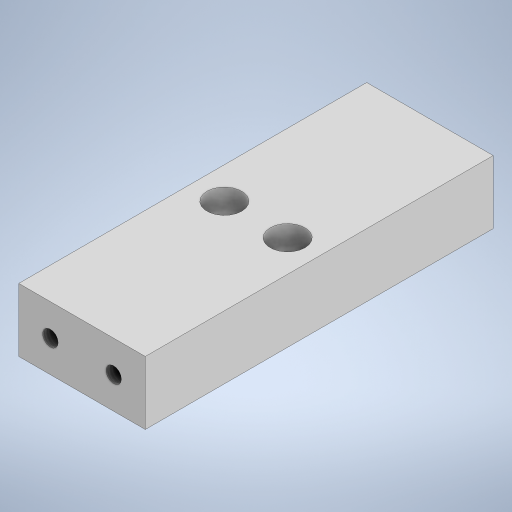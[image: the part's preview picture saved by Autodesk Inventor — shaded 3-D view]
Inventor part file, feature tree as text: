
AUTODESK INVENTOR PART (.ipt)
format: ipt  version: 2024.3 (Build 283343010, 343A)  size: 223,744 bytes
history: native  units: mm
features: sketch x4, hole x3, other x1, extrude x1, projected_geometry x1
ambient origin geometry x8: Origin, YZ Plane, XZ Plane, XY Plane, X Axis, Y Axis, Z Axis, Center Point
bodies: Body1 (feature_tree)
feature tree (10):
  other  "ソリッド1"
  extrude  "押し出し1"  Depth=20.0mm
  hole  "穴1"  [1 undecoded]
  hole  "穴2"  [1 undecoded]
  hole  "穴3"  [1 undecoded]
  sketch  "スケッチ1"
  sketch  "スケッチ2"
  sketch  "スケッチ3"
  projected_geometry  "投影ループ1"
  sketch  "スケッチ5"
note: 3 required parameter values undecoded (feature->parameter linkage not recoverable at this tier; creation-order binding heuristic only, values carry confidence <= 0.55)
